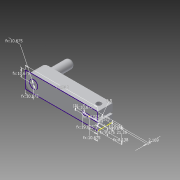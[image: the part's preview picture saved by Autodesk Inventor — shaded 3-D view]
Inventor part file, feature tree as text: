
AUTODESK INVENTOR PART (.ipt)
format: ipt  version: 2014 (Build 180170000, 170)  size: 148,480 bytes
history: native  units: mm
features: extrude x3, fillet x3, other x2, hole x2
ambient origin geometry x8: Origin, YZ Plane, XZ Plane, XY Plane, X Axis, Y Axis, Z Axis, Center Point
bodies: Solid1 (feature_tree)
feature tree (10):
  other  "Bottom"
  extrude  "Extrusion1"  Depth=10.675mm
  extrude  "Extrusion2"  Depth=93.2mm
  hole  "Hole1"  [1 undecoded]
  other  "Side"
  hole  "Hole2"  [1 undecoded]
  extrude  "Extrusion3"  Depth=9.175mm
  fillet  "Fillet1"  Radius=3.0mm
  fillet  "Fillet2"  Radius=19.025mm
  fillet  "Fillet3"  Radius=10.675mm
note: 2 required parameter values undecoded (feature->parameter linkage not recoverable at this tier; creation-order binding heuristic only, values carry confidence <= 0.55)
